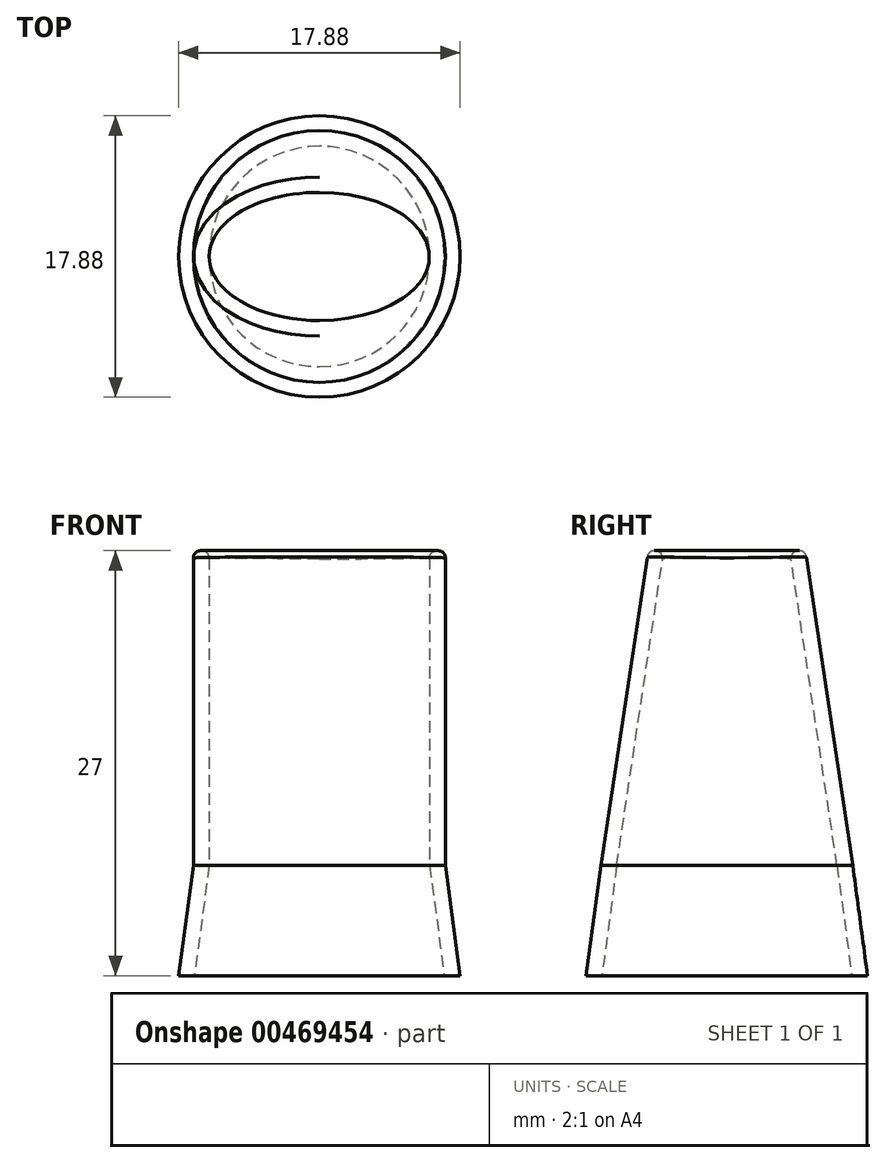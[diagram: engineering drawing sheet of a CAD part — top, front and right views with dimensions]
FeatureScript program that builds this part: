
annotation { "Feature Type Name" : "Feature", "Feature Type Description" : "" }
export const myFeature = defineFeature(function(context is Context, id is Id, definition is map)
    precondition{}
    {
        {
            var Q0;
            Q0=qCreatedBy(makeId("Top.planeOp"),FACE);
            var sketch = newSketch(context, id + "F0", { "sketchPlane" : qUnion([Q0])});
            skCircle(sketch, "E0", {"center": v(0, 0) * mm, "radius": 7.94 * mm});
            skCircle(sketch, "E1", {"center": v(0, 0) * mm, "radius": 8.94 * mm});
            skLineSegment(sketch, "E2", {"start": v(0, 8.94) * mm, "end": v(0, 7.94) * mm});
            skLineSegment(sketch, "E3.trimOffspring", {"start": v(0, -7.94) * mm, "end": v(0, -8.94) * mm});
            skSolve(sketch);
        }
        {
            var Q0;
            Q0=qCreatedBy(makeId("Top.planeOp"),FACE);
            cPlane(context, id + "F1", {"entities" : qUnion([Q0]), "cplaneType" : CPlaneType.OFFSET, "offset" : 7 * mm, "width" : 150 * mm, "height" : 150 * mm});
        }
        {
            var Q0;
            Q0=qCreatedBy(id+"F1.planeOp",FACE);
            var sketch = newSketch(context, id + "F2", { "sketchPlane" : qUnion([Q0])});
            skCircle(sketch, "E4", {"center": v(0, 0) * mm, "radius": 8 * mm});
            skCircle(sketch, "E5", {"center": v(0, 0) * mm, "radius": 7 * mm});
            skLineSegment(sketch, "E6", {"start": v(0, 8) * mm, "end": v(0, 7) * mm});
            skLineSegment(sketch, "E7.trimOffspring", {"start": v(0, -7) * mm, "end": v(0, -8) * mm});
            skSolve(sketch);
        }
        {
            var Q0;
            {var subQ0=sQuery(id+"F2.wireOp",EDGE,"E6");Q0=makeQuery(id+"F2.imprint","IMPRINT",FACE,{"disambiguationData":[TD([[makeQuery(id+"F2.imprint","IMPRINT",EDGE,{"derivedFrom":subQ0}),1.0]])]});}
            var Q1;
            {var subQ0=sQuery(id+"F0.wireOp",EDGE,"E2");Q1=makeQuery(id+"F0.imprint","IMPRINT",FACE,{"disambiguationData":[TD([[makeQuery(id+"F0.imprint","IMPRINT",EDGE,{"derivedFrom":subQ0}),1.0]])]});}
            loft(context, id + "F3", {"sheetProfilesArray" : [{ "sheetProfileEntities" : qUnion([Q0]) }, { "sheetProfileEntities" : qUnion([Q1]) }]});
        }
        {
            var Q1;
            {var subQ0=sQuery(id+"F0.wireOp",EDGE,"E2");Q1=makeQuery(id+"F0.imprint","IMPRINT",FACE,{"disambiguationData":[TD([[makeQuery(id+"F0.imprint","IMPRINT",EDGE,{"derivedFrom":subQ0}),-1.0]])]});}
            var Q2;
            {var subQ0=sQuery(id+"F2.wireOp",EDGE,"E6");Q2=makeQuery(id+"F2.imprint","IMPRINT",FACE,{"disambiguationData":[TD([[makeQuery(id+"F2.imprint","IMPRINT",EDGE,{"derivedFrom":subQ0}),-1.0]])]});}
            loft(context, id + "F4", {"operationType" : NewBodyOperationType.ADD, "sheetProfilesArray" : [{ "sheetProfileEntities" : qUnion([Q1]) }, { "sheetProfileEntities" : qUnion([Q2]) }]});
        }
        {
            var Q0;
            {var subQ0=sQuery(id+"F2.wireOp",EDGE,"E6");Q0=makeQuery(id+"F2.imprint","IMPRINT",FACE,{"disambiguationData":[TD([[makeQuery(id+"F2.imprint","IMPRINT",EDGE,{"derivedFrom":subQ0}),1.0]])]});}
            cPlane(context, id + "F5", {"entities" : qUnion([Q0]), "cplaneType" : CPlaneType.OFFSET, "offset" : 20 * mm, "width" : 150 * mm, "height" : 150 * mm});
        }
        {
            var Q0;
            Q0=qCreatedBy(id+"F5.planeOp",FACE);
            var sketch = newSketch(context, id + "F6", { "sketchPlane" : qUnion([Q0])});
            skEllipse(sketch, "E8", {"center": v(0, 0) * mm, "majorRadius": 8 * mm, "minorRadius": 5 * mm, "majorAxis": v(1, 0)});
            skEllipse(sketch, "E9", {"center": v(0, 0) * mm, "majorRadius": 7 * mm, "minorRadius": 4 * mm, "majorAxis": v(1, 0)});
            skLineSegment(sketch, "E10", {"start": v(0, 5) * mm, "end": v(0, 4) * mm});
            skLineSegment(sketch, "E11.trimOffspring", {"start": v(0, -4) * mm, "end": v(0, -5) * mm});
            skSolve(sketch);
        }
        {
            var Q1;
            {var subQ0=sQuery(id+"F2.wireOp",EDGE,"E6");Q1=makeQuery(id+"F2.imprint","IMPRINT",FACE,{"disambiguationData":[TD([[makeQuery(id+"F2.imprint","IMPRINT",EDGE,{"derivedFrom":subQ0}),-1.0]])]});}
            var Q2;
            {var subQ0=sQuery(id+"F6.wireOp",EDGE,"E10");Q2=makeQuery(id+"F6.imprint","IMPRINT",FACE,{"disambiguationData":[TD([[makeQuery(id+"F6.imprint","IMPRINT",EDGE,{"derivedFrom":subQ0}),-1.0]])]});}
            loft(context, id + "F7", {"operationType" : NewBodyOperationType.ADD, "sheetProfilesArray" : [{ "sheetProfileEntities" : qUnion([Q1]) }, { "sheetProfileEntities" : qUnion([Q2]) }]});
        }
        {
            var Q1;
            {var subQ0=sQuery(id+"F6.wireOp",EDGE,"E10");Q1=makeQuery(id+"F6.imprint","IMPRINT",FACE,{"disambiguationData":[TD([[makeQuery(id+"F6.imprint","IMPRINT",EDGE,{"derivedFrom":subQ0}),1.0]])]});}
            var Q2;
            {var subQ0=sQuery(id+"F2.wireOp",EDGE,"E6");Q2=makeQuery(id+"F2.imprint","IMPRINT",FACE,{"disambiguationData":[TD([[makeQuery(id+"F2.imprint","IMPRINT",EDGE,{"derivedFrom":subQ0}),1.0]])]});}
            loft(context, id + "F8", {"operationType" : NewBodyOperationType.ADD, "sheetProfilesArray" : [{ "sheetProfileEntities" : qUnion([Q1]) }, { "sheetProfileEntities" : qUnion([Q2]) }]});
        }
        {
            var Q0;
            Q0=makeQuery(id+"F8.opLoft","MID_CAP_EDGE",EDGE,{"disambiguationData":[OSD([sQuery(id+"F6.wireOp",EDGE,"E9"),sQuery(id+"F6.wireOp",EDGE,"E10"),sQuery(id+"F6.wireOp",EDGE,"E11.trimOffspring")])],"capPos":0.0});
            var Q1;
            Q1=makeQuery(id+"F8.opLoft","MID_CAP_EDGE",EDGE,{"disambiguationData":[OSD([sQuery(id+"F6.wireOp",EDGE,"E8"),sQuery(id+"F6.wireOp",EDGE,"E10"),sQuery(id+"F6.wireOp",EDGE,"E11.trimOffspring")])],"capPos":0.0});
            fillet(context, id + "F9", {"entities" : qUnion([Q0, Q1]), "radius" : 0.45 * mm, "tangentPropagation" : true, "allowEdgeOverflow" : false});
        }
    });
